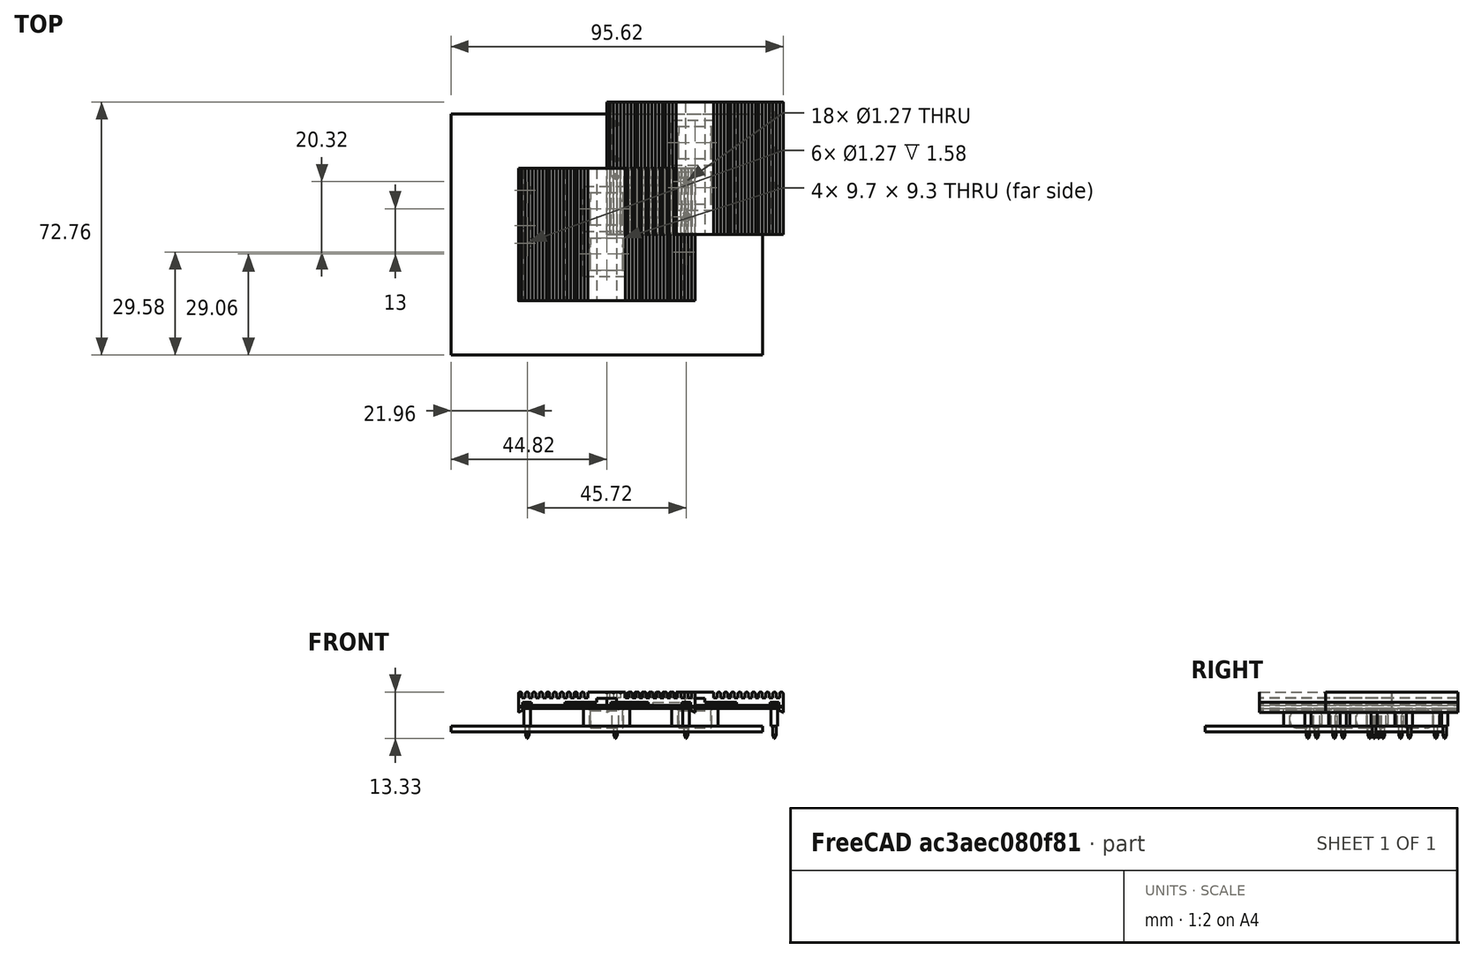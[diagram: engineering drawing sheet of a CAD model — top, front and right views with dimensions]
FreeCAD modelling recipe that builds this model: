
FCSTD DOCUMENT  (FreeCAD 0.18R16131 (Git))
Label: Meanwell_NSD15-S
License: All rights reserved
LicenseURL: http://en.wikipedia.org/wiki/All_rights_reserved
objects: Part::Feature×14, Part::Cylinder×12, Part::Box×7, Part::Cone×6, Part::MultiFuse×6, Part::FeaturePython×6, Part::Cut×2, Part::Fillet×2, Part::Extrusion×1, App::DocumentObjectGroup×1, App::Part×1
note: 56 computed .brp shape members not serialized (recipe doc carries the construction recipe); baked Part::Feature solids carry a one-line shape summary decoded from their .brp

FEATURE [Part::Feature] path4531
  shape: bbox 50.8 x 5.84 x 2e-07 mm, 0 faces, 0 solids (baked)
FEATURE [Part::Extrusion] Extrude  label="Heatsink"
  Base = -> path4531
  Dir = (0,0,1)
  DirMode = 2
  FaceMakerClass = Part::FaceMakerBullseye
  LengthFwd = 38.1
  LengthRev = 0
  Placement = pos=(0,19.05,300.98) rot=(1,0,0;1.5708rad)
  Solid = true
  Symmetric = true
FEATURE [Part::Box] Box  label="Cube"
  AttacherType = Attacher::AttachEngine3D
  Height = 0.95
  Length = 49
  Placement = pos=(0.9,0,5.05) rot=(0,0,1;0rad)
  Width = 38.1
FEATURE [Part::Cylinder] Cylinder
  Angle = 360
  AttacherType = Attacher::AttachEngine3D
  Height = 5.05
  Placement = pos=(2.54,0,0) rot=(0,0,1;0rad)
  Radius = 0.9
FEATURE [Part::Cylinder] Cylinder001
  Angle = 360
  AttacherType = Attacher::AttachEngine3D
  Height = 2.51
  Placement = pos=(2.54,0,-2.51) rot=(0,0,1;0rad)
  Radius = 0.5
FEATURE [Part::Cone] Cone
  Angle = 360
  AttacherType = Attacher::AttachEngine3D
  Height = 1
  Placement = pos=(2.54,0,-3.51) rot=(0,0,1;0rad)
  Radius1 = 0.1
  Radius2 = 0.5
FEATURE [Part::MultiFuse] Fusion  label="Pin 1"
  Placement = pos=(0,16.51,0) rot=(0,0,1;0rad)
  Shapes = -> [Cylinder,Cylinder001,Cone]
FEATURE [Part::Cone] Cone001
  Angle = 360
  AttacherType = Attacher::AttachEngine3D
  Height = 1
  Placement = pos=(2.54,0,-3.51) rot=(0,0,1;0rad)
  Radius1 = 0.1
  Radius2 = 0.5
FEATURE [Part::Cylinder] Cylinder003
  Angle = 360
  AttacherType = Attacher::AttachEngine3D
  Height = 2.51
  Placement = pos=(2.54,0,-2.51) rot=(0,0,1;0rad)
  Radius = 0.5
FEATURE [Part::Cylinder] Cylinder004
  Angle = 360
  AttacherType = Attacher::AttachEngine3D
  Height = 5.05
  Placement = pos=(2.54,0,0) rot=(0,0,1;0rad)
  Radius = 0.9
FEATURE [Part::MultiFuse] Fusion001  label="Pin 2"
  Placement = pos=(0,21.59,0) rot=(0,0,1;0rad)
  Shapes = -> [Cylinder004,Cylinder003,Cone001]
FEATURE [Part::Cone] Cone002
  Angle = 360
  AttacherType = Attacher::AttachEngine3D
  Height = 1
  Placement = pos=(2.54,0,-3.51) rot=(0,0,1;0rad)
  Radius1 = 0.1
  Radius2 = 0.5
FEATURE [Part::Cylinder] Cylinder005
  Angle = 360
  AttacherType = Attacher::AttachEngine3D
  Height = 2.51
  Placement = pos=(2.54,0,-2.51) rot=(0,0,1;0rad)
  Radius = 0.5
FEATURE [Part::Cylinder] Cylinder006
  Angle = 360
  AttacherType = Attacher::AttachEngine3D
  Height = 5.05
  Placement = pos=(2.54,0,0) rot=(0,0,1;0rad)
  Radius = 0.9
FEATURE [Part::MultiFuse] Fusion002  label="Pin 4"
  Placement = pos=(0,31.75,0) rot=(0,0,1;0rad)
  Shapes = -> [Cylinder006,Cylinder005,Cone002]
FEATURE [Part::Cone] Cone003
  Angle = 360
  AttacherType = Attacher::AttachEngine3D
  Height = 1
  Placement = pos=(2.54,0,-3.51) rot=(0,0,1;0rad)
  Radius1 = 0.1
  Radius2 = 0.5
FEATURE [Part::Cylinder] Cylinder007
  Angle = 360
  AttacherType = Attacher::AttachEngine3D
  Height = 2.51
  Placement = pos=(2.54,0,-2.51) rot=(0,0,1;0rad)
  Radius = 0.5
FEATURE [Part::Cylinder] Cylinder008
  Angle = 360
  AttacherType = Attacher::AttachEngine3D
  Height = 5.05
  Placement = pos=(2.54,0,0) rot=(0,0,1;0rad)
  Radius = 0.9
FEATURE [Part::MultiFuse] Fusion003  label="Pin 6"
  Placement = pos=(45.72,13.97,0) rot=(0,0,1;0rad)
  Shapes = -> [Cylinder008,Cylinder007,Cone003]
FEATURE [Part::Cone] Cone004
  Angle = 360
  AttacherType = Attacher::AttachEngine3D
  Height = 1
  Placement = pos=(2.54,0,-3.51) rot=(0,0,1;0rad)
  Radius1 = 0.1
  Radius2 = 0.5
FEATURE [Part::Cylinder] Cylinder009
  Angle = 360
  AttacherType = Attacher::AttachEngine3D
  Height = 5.05
  Placement = pos=(2.54,0,0) rot=(0,0,1;0rad)
  Radius = 0.9
FEATURE [Part::Cylinder] Cylinder010
  Angle = 360
  AttacherType = Attacher::AttachEngine3D
  Height = 2.51
  Placement = pos=(2.54,0,-2.51) rot=(0,0,1;0rad)
  Radius = 0.5
FEATURE [Part::MultiFuse] Fusion004  label="Pin 7"
  Placement = pos=(45.72,24.13,0) rot=(0,0,1;0rad)
  Shapes = -> [Cylinder009,Cylinder010,Cone004]
FEATURE [Part::Cone] Cone005
  Angle = 360
  AttacherType = Attacher::AttachEngine3D
  Height = 1
  Placement = pos=(2.54,0,-3.51) rot=(0,0,1;0rad)
  Radius1 = 0.1
  Radius2 = 0.5
FEATURE [Part::Cylinder] Cylinder011
  Angle = 360
  AttacherType = Attacher::AttachEngine3D
  Height = 5.05
  Placement = pos=(2.54,0,0) rot=(0,0,1;0rad)
  Radius = 0.9
FEATURE [Part::Cylinder] Cylinder012
  Angle = 360
  AttacherType = Attacher::AttachEngine3D
  Height = 2.51
  Placement = pos=(2.54,0,-2.51) rot=(0,0,1;0rad)
  Radius = 0.5
FEATURE [Part::MultiFuse] Fusion005  label="Pin 8"
  Placement = pos=(45.72,34.29,0) rot=(0,0,1;0rad)
  Shapes = -> [Cylinder011,Cylinder012,Cone005]
FEATURE [Part::Box] Box001  label="Cube001"
  AttacherType = Attacher::AttachEngine3D
  Height = 5.1
  Length = 13.3
  Width = 12.9
FEATURE [Part::Box] Box002  label="Cube002"
  AttacherType = Attacher::AttachEngine3D
  Height = 5.1
  Length = 9.7
  Placement = pos=(1.8,1.8,0) rot=(0,0,1;0rad)
  Width = 9.3
FEATURE [Part::Cut] Cut
  Base = -> Box001
  Placement = pos=(18.75,7,0) rot=(0,0,1;0rad)
  Tool = -> Box002
FEATURE [Part::Box] Box003  label="Cube003"
  AttacherType = Attacher::AttachEngine3D
  Height = 5
  Length = 9.3
  Width = 9.3
FEATURE [Part::Fillet] Fillet
  Base = -> Box003
  Edges = 4 edges r=2: [Edge9,Edge10,Edge11,Edge12]
  Placement = pos=(20.75,8.8,-0.5) rot=(0,0,1;0rad)
FEATURE [Part::Box] Box004  label="Cube004"
  AttacherType = Attacher::AttachEngine3D
  Height = 5.1
  Length = 9.7
  Placement = pos=(1.8,1.8,0) rot=(0,0,1;0rad)
  Width = 9.3
FEATURE [Part::Box] Box005  label="Cube005"
  AttacherType = Attacher::AttachEngine3D
  Height = 5.1
  Length = 13.3
  Width = 12.9
FEATURE [Part::Cut] Cut001
  Base = -> Box005
  Placement = pos=(18.75,20,0) rot=(0,0,1;0rad)
  Tool = -> Box004
FEATURE [Part::Box] Box006  label="Cube006"
  AttacherType = Attacher::AttachEngine3D
  Height = 5
  Length = 9.3
  Width = 9.3
FEATURE [Part::Fillet] Fillet001
  Base = -> Box006
  Edges = 4 edges r=2: [Edge9,Edge10,Edge11,Edge12]
  Placement = pos=(20.75,21.8,-0.5) rot=(0,0,1;0rad)
FEATURE [Part::FeaturePython] FCrtYd_lines  label="FCrtYd"  # a2plus imported part (geometry in sourceFile) (typed FeaturePython)
  fixedPosition = true
FEATURE [Part::FeaturePython] FFab_lines  label="FFab"  # a2plus imported part (geometry in sourceFile) (typed FeaturePython)
  fixedPosition = true
FEATURE [Part::FeaturePython] TopPads  # a2plus imported part (geometry in sourceFile) (typed FeaturePython)
  fixedPosition = true
FEATURE [Part::FeaturePython] BotPads  # a2plus imported part (geometry in sourceFile) (typed FeaturePython)
  fixedPosition = true
FEATURE [Part::FeaturePython] THPs  label="PTHs"  # a2plus imported part (geometry in sourceFile) (typed FeaturePython)
  fixedPosition = true
FEATURE [Part::FeaturePython] newPCB  label="Pcb"  # a2plus imported part (geometry in sourceFile) (typed FeaturePython)
  fixedPosition = true
FEATURE [App::DocumentObjectGroup] DCDC_CONVERTER_MEANWELL_fp
  Group = -> [FCrtYd_lines,FFab_lines,TopPads,BotPads,THPs,newPCB]
FEATURE [App::Part] Part  label="Meanwell_NSD15-S"
  Group = -> [path4531,Extrude,Box,Cone,Cylinder001,Cylinder,Fusion,Cone001,Cylinder003,Cylinder004,Fusion001,Cone002,Cylinder005,Cylinder006,Fusion002,Cone003,Cylinder008,Cylinder007,Fusion003,Cone004,Cylinder010,Cylinder009,Fusion004,Cone005,Cylinder012,Cylinder011,Fusion005,Box002,Box001,Cut,Box003,Fillet,Box004,Box005,Cut001,Box006,Fillet001]
  Origin = -> Origin
FEATURE [Part::Feature] Extrude_cp  label="Heatsink_cp"
  Placement = pos=(0,19.05,300.98) rot=(1,0,0;1.5708rad)
  shape: bbox 50.8 x 38.1 x 5.84 mm, 136 faces (baked)
FEATURE [Part::Feature] Box_cp  label="Cube_cp"
  Placement = pos=(0.9,0,5.05) rot=(0,0,1;0rad)
  shape: bbox 49 x 38.1 x 0.95 mm, 6 faces (baked)
FEATURE [Part::Feature] Fusion_cp  label="Pin 1_cp"
  Placement = pos=(0,16.51,0) rot=(0,0,1;0rad)
  shape: bbox 1.8 x 1.8 x 8.56 mm, 6 faces (baked)
FEATURE [Part::Feature] Fusion001_cp  label="Pin 2_cp"
  Placement = pos=(0,21.59,0) rot=(0,0,1;0rad)
  shape: bbox 1.8 x 1.8 x 8.56 mm, 6 faces (baked)
FEATURE [Part::Feature] Fusion002_cp  label="Pin 4_cp"
  Placement = pos=(0,31.75,0) rot=(0,0,1;0rad)
  shape: bbox 1.8 x 1.8 x 8.56 mm, 6 faces (baked)
FEATURE [Part::Feature] Fusion003_cp  label="Pin 6_cp"
  Placement = pos=(45.72,13.97,0) rot=(0,0,1;0rad)
  shape: bbox 1.8 x 1.8 x 8.56 mm, 6 faces (baked)
FEATURE [Part::Feature] Fusion004_cp  label="Pin 7_cp"
  Placement = pos=(45.72,24.13,0) rot=(0,0,1;0rad)
  shape: bbox 1.8 x 1.8 x 8.56 mm, 6 faces (baked)
FEATURE [Part::Feature] Fusion005_cp  label="Pin 8_cp"
  Placement = pos=(45.72,34.29,0) rot=(0,0,1;0rad)
  shape: bbox 1.8 x 1.8 x 8.56 mm, 6 faces (baked)
FEATURE [Part::Feature] Cut_cp
  Placement = pos=(18.75,7,0) rot=(0,0,1;0rad)
  shape: bbox 13.3 x 12.9 x 5.1 mm, 10 faces (baked)
FEATURE [Part::Feature] Fillet_cp
  Placement = pos=(20.75,8.8,-0.5) rot=(0,0,1;0rad)
  shape: bbox 9.3 x 9.3 x 5 mm, 10 faces (baked)
FEATURE [Part::Feature] Cut001_cp
  Placement = pos=(18.75,20,0) rot=(0,0,1;0rad)
  shape: bbox 13.3 x 12.9 x 5.1 mm, 10 faces (baked)
FEATURE [Part::Feature] Fillet001_cp
  Placement = pos=(20.75,21.8,-0.5) rot=(0,0,1;0rad)
  shape: bbox 9.3 x 9.3 x 5 mm, 10 faces (baked)
FEATURE [Part::Feature] Shape001  label="Meanwell_NSD15_S_cp"
  shape: bbox 50.8 x 38.1 x 13.33 mm, 218 faces, 12 solids (baked)
